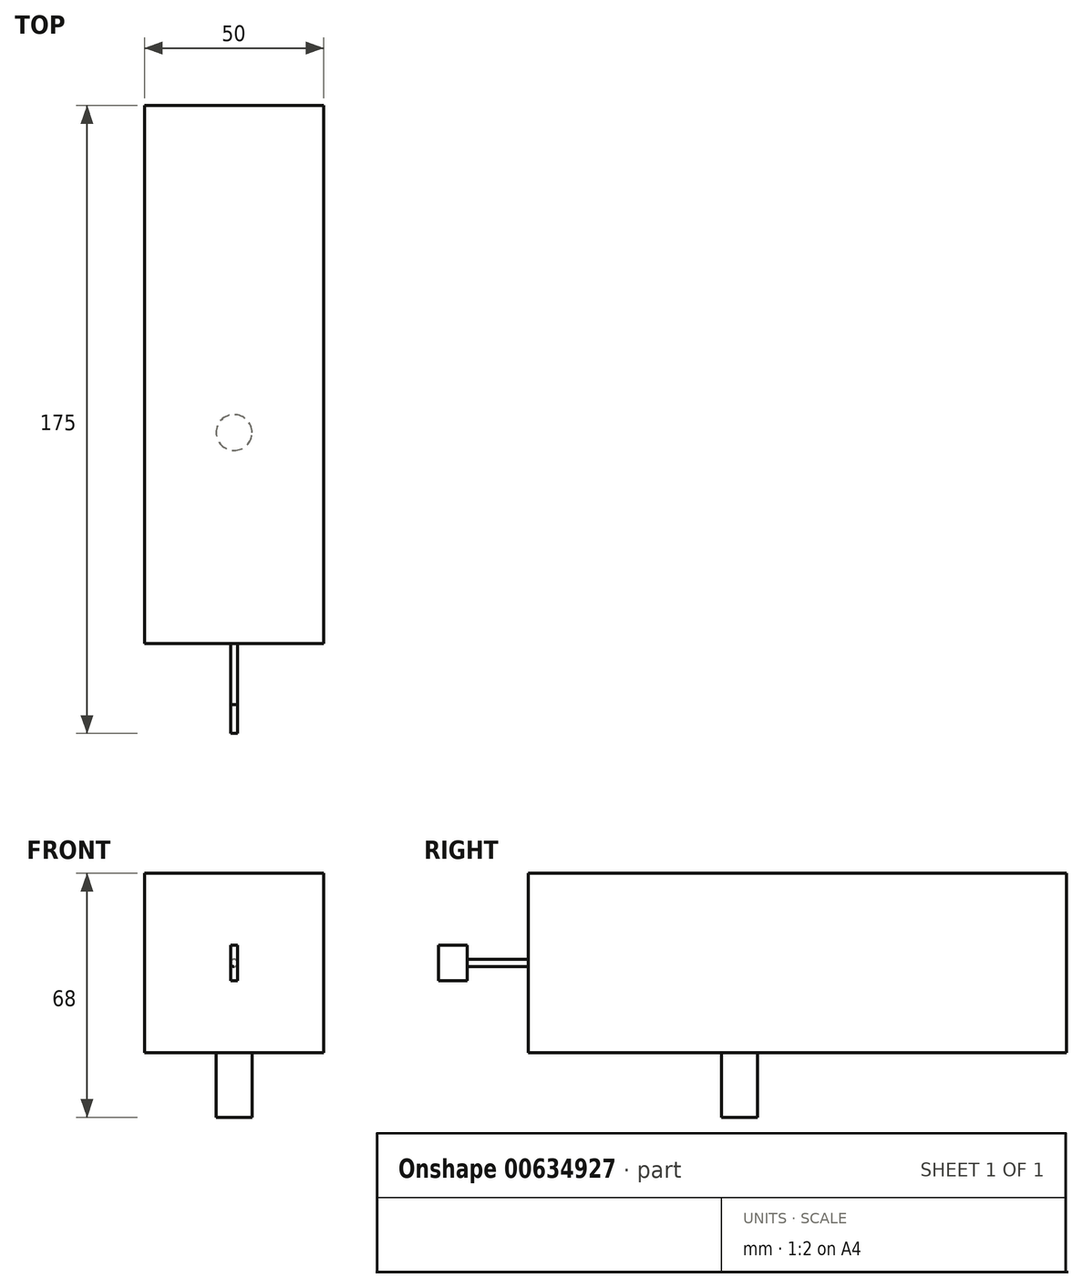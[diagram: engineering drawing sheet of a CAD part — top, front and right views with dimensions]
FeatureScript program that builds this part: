
annotation { "Feature Type Name" : "Feature", "Feature Type Description" : "" }
export const myFeature = defineFeature(function(context is Context, id is Id, definition is map)
    precondition{}
    {
        {
            var Q0;
            Q0=qCreatedBy(makeId("Front.planeOp"),FACE);
            var sketch = newSketch(context, id + "F0", { "sketchPlane" : qUnion([Q0])});
            skLineSegment(sketch, "E0.bottom", {"start": v(-25, 0) * mm, "end": v(25, 0) * mm});
            skLineSegment(sketch, "E0.top", {"start": v(-25, 50) * mm, "end": v(25, 50) * mm});
            skLineSegment(sketch, "E0.left", {"start": v(-25, 0) * mm, "end": v(-25, 50) * mm});
            skLineSegment(sketch, "E0.right", {"start": v(25, 0) * mm, "end": v(25, 50) * mm});
            skSolve(sketch);
        }
        {
            var Q0;
            Q0 = qSketchRegion(id + "F0", true);
            extrude(context, id + "F1", {"entities" : qUnion([Q0]), "depth" : 150 * mm, "offsetDistance" : 25 * mm});
        }
        {
            var Q0;
            Q0=makeQuery(id+"F1.opExtrude","CAP_FACE",FACE,{"disambiguationData":[OSD([sQuery(id+"F0.wireOp",EDGE,"E0.bottom"),sQuery(id+"F0.wireOp",EDGE,"E0.top"),sQuery(id+"F0.wireOp",EDGE,"E0.left"),sQuery(id+"F0.wireOp",EDGE,"E0.right")])],"isStart":false});
            var sketch = newSketch(context, id + "F2", { "sketchPlane" : qUnion([Q0])});
            skCircle(sketch, "E1", {"center": v(0, 25) * mm, "radius": 1 * mm});
            skSolve(sketch);
        }
        {
            var Q0;
            Q0 = qSketchRegion(id + "F2", true);
            extrude(context, id + "F3", {"entities" : qUnion([Q0]), "operationType" : NewBodyOperationType.ADD, "depth" : 25 * mm, "offsetDistance" : 25 * mm});
        }
        {
            var Q0;
            Q0=makeQuery(id+"F3.opExtrude","CAP_FACE",FACE,{"disambiguationData":[OSD([sQuery(id+"F2.wireOp",EDGE,"E1")])],"isStart":false});
            var sketch = newSketch(context, id + "F4", { "sketchPlane" : qUnion([Q0])});
            skLineSegment(sketch, "E2.bottom", {"start": v(-1, 30) * mm, "end": v(1, 30) * mm});
            skLineSegment(sketch, "E2.top", {"start": v(-1, 20) * mm, "end": v(1, 20) * mm});
            skLineSegment(sketch, "E2.left", {"start": v(-1, 30) * mm, "end": v(-1, 20) * mm});
            skLineSegment(sketch, "E2.right", {"start": v(1, 30) * mm, "end": v(1, 20) * mm});
            skSolve(sketch);
        }
        {
            var Q0;
            Q0 = qSketchRegion(id + "F4", true);
            extrude(context, id + "F5", {"entities" : qUnion([Q0]), "operationType" : NewBodyOperationType.ADD, "oppositeDirection" : true, "depth" : 8 * mm, "offsetDistance" : 25 * mm});
        }
        {
            var Q0;
            Q0=makeQuery(id+"F1.opExtrude","SWEPT_FACE",FACE,{"disambiguationData":[OSD([sQuery(id+"F0.wireOp",EDGE,"E0.bottom")])]});
            var sketch = newSketch(context, id + "F6", { "sketchPlane" : qUnion([Q0])});
            skCircle(sketch, "E3", {"center": v(0, 91.15) * mm, "radius": 5 * mm});
            skSolve(sketch);
        }
        {
            var Q0;
            Q0 = qSketchRegion(id + "F6", true);
            extrude(context, id + "F7", {"entities" : qUnion([Q0]), "operationType" : NewBodyOperationType.ADD, "depth" : 18 * mm, "offsetDistance" : 25 * mm});
        }
    });
